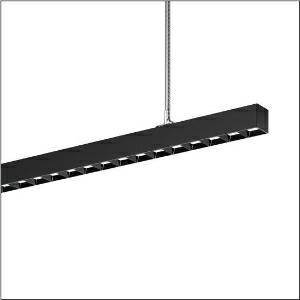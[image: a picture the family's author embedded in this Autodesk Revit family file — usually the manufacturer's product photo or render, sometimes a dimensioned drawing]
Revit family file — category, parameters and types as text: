
# Revit family: silica_r__21_51mx31tctdb_123f
name_source: partatom
category: Lighting Fixtures
units: mm (PartAtom-declared; Revit-internal decimal feet)

## family parameters
Cut with Voids When Loaded = No
Host = Face
Light Source = No
Part Type = Normal
Room Calculation Point = No
Round Connector Dimension = Use Diameter
Shared = No

## types (1)
- --- (1 x LED, 15550 lm, 133.9 W, 6500K)
    Apparent Load = 134 VA
    CIE Flux Codes = 85 99 100 60 100
    Color Rendering = 80
    Color Temperature = 6500K
    Default Elevation = 1800 mm
    Description = Silica® 21, office luminaire, primary light control with darklight reflector, of PMMA, black, CAT 2 (L<= 3000cd/m²), light emission: direct/indirect distribution, primary light characteristic: symmetric, installation type: suspended mounting, LED, rated luminous flux: 15.550lm, luminous efficacy: 111lm/W, light colour: 8tw, colour temperature: 2700..6500K, control gear: DALI DT8, with terminal, 3+2-pole, max. 2.5mm², mains connection: 220..240V, AC, 50/60Hz, rated input power: 140.6W, luminaire housing, of aluminium, matt jet black (RAL 9005), length: 3.004mm, width: 53mm, height: 53mm, protection rating (complete): IP20, insulation class (complete): insulation class I (protective earthing), certification: CE, permissible operating ambient temperature: 0..+35°C, standard: EN 50419, packaging unit: 1 piece
    Height = 53 mm
    Lamp = 1 x LED
    Lamp Light Flux = 15550 lm
    Lamp Power = 133.9 W
    Lamp count = 1
    Length = 3004 mm
    Luminous efficacy = 116 lm/W
    Manufacturer = Siteco
    ModVariant = No
    Model = 51MX31TCTDB
    Mounting Place = Ceiling
    Mounting Type = Pendant
    Number of Poles = 1
    OnlyDefault = Yes
    Power Factor = 1
    Product Name = Silica® 21
    Product group = office luminaire | ceiling pendant
    ProductGroupID = 904
    Protection Class = Protection class I
    Protection Degree = IP 20
    RLX_Detail_Level = 1
    RLX_Emergency_Light_Flux = 0 lm
    RLX_Emergency_Type = 0
    RLX_Emergency_Type_DB = No
    RlxData = <blob elided: 63521 chars, md5=53a8bd05>
    Socket = socket
    Standby Power = 0 W
    System Light Flux = 15550 lm
    System Power = 134 W
    Type Comments = individual setting
    Type Image = l_1335852.jpg
    URL = http://relux.com
    VarID = @adj_139878
    Voltage = 0 V
    Weight = 0.00 kg
    Width = 53 mm

## geometry (parser evidence)
native form markers: Blend x4, Sweep x13
no freeform markers — native parametric forms only
